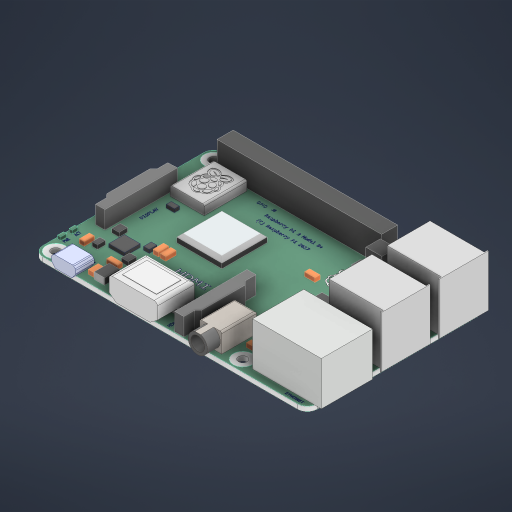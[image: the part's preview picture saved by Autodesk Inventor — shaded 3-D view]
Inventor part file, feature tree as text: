
AUTODESK INVENTOR PART (.ipt)
format: ipt  version: 2023 (Build 270158000, 158)  size: 3,770,368 bytes
history: native  units: mm
features: other x173, fillet x4, chamfer x1, extrude x1
ambient origin geometry x8: Origin, YZ Plane, XZ Plane, XY Plane, X Axis, Y Axis, Z Axis, Center Point
bodies: Solid1 (feature_tree), Solid2 (feature_tree), Solid3 (feature_tree), Solid4 (feature_tree), Solid5 (feature_tree), Solid6 (feature_tree), Solid7 (feature_tree), Solid8 (feature_tree), Solid9 (feature_tree), Solid10 (feature_tree), Solid11 (feature_tree), Solid12 (feature_tree), Solid13 (feature_tree), Solid14 (feature_tree), Solid15 (feature_tree), Solid16 (feature_tree), Solid17 (feature_tree), Solid18 (feature_tree), Solid19 (feature_tree), Solid20 (feature_tree), Solid21 (feature_tree), Solid22 (feature_tree), Solid23 (feature_tree), Solid24 (feature_tree), Solid25 (feature_tree), Solid26 (feature_tree), Solid27 (feature_tree), Solid28 (feature_tree), Solid29 (feature_tree), Solid30 (feature_tree), Solid31 (feature_tree), Solid32 (feature_tree), Solid33 (feature_tree), Solid34 (feature_tree), Solid35 (feature_tree), Solid36 (feature_tree), Solid37 (feature_tree), Solid38 (feature_tree), Solid39 (feature_tree), Solid40 (feature_tree), Solid41 (feature_tree), Solid42 (feature_tree), Solid43 (feature_tree), Solid44 (feature_tree), Solid45 (feature_tree), Solid46 (feature_tree), Solid47 (feature_tree), Solid48 (feature_tree), Solid49 (feature_tree), Solid50 (feature_tree), Solid51 (feature_tree), Solid52 (feature_tree), Solid53 (feature_tree), Solid54 (feature_tree), Solid55 (feature_tree), Solid56 (feature_tree), Solid57 (feature_tree), Solid58 (feature_tree), Solid59 (feature_tree), Solid60 (feature_tree), Solid61 (feature_tree), Solid62 (feature_tree), Solid63 (feature_tree), Solid64 (feature_tree), Solid65 (feature_tree), Solid66 (feature_tree), Solid67 (feature_tree), Solid68 (feature_tree), Solid69 (feature_tree), Solid70 (feature_tree), Solid71 (feature_tree), Solid72 (feature_tree), Solid73 (feature_tree), Solid74 (feature_tree), Solid75 (feature_tree), Solid76 (feature_tree), Solid77 (feature_tree), Solid78 (feature_tree), Solid79 (feature_tree), Solid80 (feature_tree), Solid81 (feature_tree), Solid82 (feature_tree), Solid83 (feature_tree), Solid84 (feature_tree), Solid85 (feature_tree), Solid86 (feature_tree), Solid87 (feature_tree), Solid88 (feature_tree), Solid89 (feature_tree), Solid90 (feature_tree), Solid91 (feature_tree), Solid92 (feature_tree), Solid93 (feature_tree), Solid94 (feature_tree), Solid95 (feature_tree), Solid96 (feature_tree), Solid97 (feature_tree), Solid98 (feature_tree), Solid99 (feature_tree), Solid100 (feature_tree), Solid101 (feature_tree), Solid102 (feature_tree), Solid103 (feature_tree), Solid104 (feature_tree), Solid105 (feature_tree), Solid106 (feature_tree), Solid107 (feature_tree), Solid108 (feature_tree), Solid109 (feature_tree), Solid110 (feature_tree), Solid111 (feature_tree), Solid112 (feature_tree), Solid113 (feature_tree), Solid114 (feature_tree), Solid115 (feature_tree), Solid116 (feature_tree), Solid117 (feature_tree), Solid118 (feature_tree), Solid119 (feature_tree), Solid120 (feature_tree), Solid121 (feature_tree), Solid122 (feature_tree), Solid123 (feature_tree), Solid124 (feature_tree), Solid125 (feature_tree), Solid126 (feature_tree), Solid127 (feature_tree), Solid128 (feature_tree), Solid129 (feature_tree), Solid130 (feature_tree), Solid131 (feature_tree), Solid132 (feature_tree), Solid133 (feature_tree), Solid134 (feature_tree), Solid135 (feature_tree), Solid136 (feature_tree), Solid137 (feature_tree), Solid138 (feature_tree), Solid139 (feature_tree), Solid140 (feature_tree), Solid141 (feature_tree), Solid142 (feature_tree), Solid143 (feature_tree), Solid144 (feature_tree), Solid145 (feature_tree), Solid146 (feature_tree), Solid147 (feature_tree), Solid148 (feature_tree), Solid149 (feature_tree), Solid150 (feature_tree), Solid151 (feature_tree), Solid152 (feature_tree), Solid153 (feature_tree), Solid154 (feature_tree), Solid155 (feature_tree), Solid156 (feature_tree), Solid157 (feature_tree), Solid158 (feature_tree), Solid159 (feature_tree), Solid160 (feature_tree), Solid161 (feature_tree), Solid162 (feature_tree), Solid163 (feature_tree), Solid164 (feature_tree), Solid165 (feature_tree), Solid166 (feature_tree), Solid167 (feature_tree), Solid168 (feature_tree), Solid169 (feature_tree), Solid170 (feature_tree), Solid171 (feature_tree), Solid172 (feature_tree), Solid173 (feature_tree), Solid174 (feature_tree), Solid175 (feature_tree), Solid176 (feature_tree), Solid177 (feature_tree), Solid178 (feature_tree), Solid179 (feature_tree)
feature tree (179):
  other  "Boss-Extrude4[1]"
  other  "Boss-Extrude5[1]"
  other  "Boss-Extrude5[2]"
  other  "Boss-Extrude6"
  other  "Boss-Extrude8[1]"
  other  "Boss-Extrude8[2]"
  fillet  "Fillet2"  [1 undecoded]
  fillet  "Fillet1"  [1 undecoded]
  other  "Boss-Extrude10"
  other  "Wrap1"
  chamfer  "Chamfer1"  [1 undecoded]
  fillet  "Fillet4"  [1 undecoded]
  other  "Boss-Extrude4[2]"
  extrude  "Extrude-Thin1"  [1 undecoded]
  other  "Cut-Extrude5[1]"
  other  "Boss-Extrude14[1]"
  other  "Boss-Extrude14[2]"
  other  "Boss-Extrude15[1]"
  other  "Boss-Extrude16[1]"
  other  "Boss-Extrude16[2]"
  other  "Boss-Extrude16[3]"
  other  "Boss-Extrude16[4]"
  other  "Boss-Extrude16[5]"
  other  "Boss-Extrude16[6]"
  other  "Boss-Extrude16[7]"
  other  "Boss-Extrude16[8]"
  other  "Boss-Extrude16[9]"
  other  "Boss-Extrude16[10]"
  other  "Boss-Extrude16[11]"
  other  "Boss-Extrude16[12]"
  other  "Boss-Extrude15[2]"
  other  "Boss-Extrude15[3]"
  other  "Boss-Extrude15[4]"
  other  "Boss-Extrude15[5]"
  other  "Boss-Extrude15[6]"
  other  "Boss-Extrude16[13]"
  other  "Boss-Extrude16[14]"
  other  "Boss-Extrude16[15]"
  other  "Boss-Extrude17"
  other  "Boss-Extrude15[7]"
  other  "Boss-Extrude18[1]"
  other  "Boss-Extrude18[2]"
  other  "Boss-Extrude18[3]"
  other  "Boss-Extrude18[4]"
  other  "Boss-Extrude18[5]"
  other  "Boss-Extrude18[6]"
  other  "Boss-Extrude18[7]"
  other  "Boss-Extrude18[8]"
  other  "Boss-Extrude18[9]"
  other  "Boss-Extrude18[10]"
  other  "Boss-Extrude18[11]"
  other  "Boss-Extrude18[12]"
  other  "Boss-Extrude18[13]"
  other  "Boss-Extrude18[14]"
  other  "Boss-Extrude18[15]"
  other  "Boss-Extrude18[16]"
  other  "Boss-Extrude18[17]"
  other  "Boss-Extrude18[18]"
  other  "Boss-Extrude18[19]"
  other  "Boss-Extrude18[20]"
  other  "Boss-Extrude18[21]"
  other  "Boss-Extrude18[22]"
  other  "Boss-Extrude18[23]"
  other  "Boss-Extrude18[24]"
  other  "Boss-Extrude18[25]"
  other  "Boss-Extrude18[26]"
  other  "Boss-Extrude18[27]"
  other  "Boss-Extrude18[28]"
  other  "Boss-Extrude18[29]"
  other  "Boss-Extrude18[30]"
  other  "Boss-Extrude18[31]"
  other  "Boss-Extrude18[32]"
  other  "Boss-Extrude18[33]"
  other  "Boss-Extrude18[34]"
  other  "Boss-Extrude18[35]"
  other  "Boss-Extrude18[36]"
  other  "Boss-Extrude18[37]"
  other  "Boss-Extrude18[38]"
  other  "Boss-Extrude18[39]"
  other  "Boss-Extrude18[40]"
  other  "Boss-Extrude18[41]"
  other  "Boss-Extrude18[42]"
  other  "Boss-Extrude18[43]"
  other  "Boss-Extrude18[44]"
  other  "Boss-Extrude18[45]"
  other  "Boss-Extrude18[46]"
  other  "Boss-Extrude18[47]"
  other  "Boss-Extrude19"
  other  "Boss-Extrude21[1]"
  other  "Boss-Extrude21[2]"
  other  "Boss-Extrude21[3]"
  other  "Boss-Extrude21[4]"
  other  "Boss-Extrude21[5]"
  other  "Boss-Extrude21[6]"
  other  "Boss-Extrude21[7]"
  other  "Boss-Extrude21[8]"
  other  "Boss-Extrude21[9]"
  other  "Boss-Extrude21[10]"
  other  "Boss-Extrude21[11]"
  other  "Boss-Extrude21[12]"
  other  "Boss-Extrude21[13]"
  other  "Boss-Extrude21[14]"
  other  "Boss-Extrude21[15]"
  other  "Boss-Extrude21[16]"
  other  "Boss-Extrude21[17]"
  other  "Boss-Extrude21[18]"
  other  "Boss-Extrude21[19]"
  other  "Boss-Extrude21[20]"
  other  "Boss-Extrude21[21]"
  other  "Boss-Extrude21[22]"
  other  "Boss-Extrude21[23]"
  other  "Boss-Extrude21[24]"
  other  "Boss-Extrude21[25]"
  other  "Boss-Extrude21[26]"
  other  "Boss-Extrude21[27]"
  other  "Boss-Extrude21[28]"
  other  "Boss-Extrude21[29]"
  other  "Boss-Extrude21[30]"
  other  "Boss-Extrude21[31]"
  other  "Boss-Extrude21[32]"
  other  "Boss-Extrude21[33]"
  other  "Boss-Extrude21[34]"
  other  "Boss-Extrude21[35]"
  other  "Boss-Extrude21[36]"
  other  "Boss-Extrude21[37]"
  other  "Boss-Extrude21[38]"
  other  "Boss-Extrude21[39]"
  other  "Boss-Extrude21[40]"
  other  "Boss-Extrude21[41]"
  other  "Boss-Extrude21[42]"
  other  "Boss-Extrude21[43]"
  other  "Boss-Extrude21[44]"
  other  "Boss-Extrude21[45]"
  other  "Boss-Extrude21[46]"
  other  "Boss-Extrude21[47]"
  other  "Boss-Extrude21[48]"
  other  "Boss-Extrude21[49]"
  other  "Boss-Extrude21[50]"
  other  "Boss-Extrude21[51]"
  other  "Boss-Extrude21[52]"
  other  "Boss-Extrude21[53]"
  other  "Boss-Extrude21[54]"
  other  "Boss-Extrude21[55]"
  other  "Boss-Extrude21[56]"
  other  "Boss-Extrude21[57]"
  other  "Boss-Extrude21[58]"
  other  "Boss-Extrude21[59]"
  other  "Boss-Extrude21[60]"
  other  "Boss-Extrude21[61]"
  other  "Boss-Extrude21[62]"
  other  "Boss-Extrude21[63]"
  other  "Boss-Extrude21[64]"
  other  "Boss-Extrude21[65]"
  other  "Boss-Extrude21[66]"
  other  "Boss-Extrude21[67]"
  other  "Boss-Extrude21[68]"
  other  "Boss-Extrude21[69]"
  other  "Boss-Extrude21[70]"
  other  "Boss-Extrude21[71]"
  other  "Boss-Extrude21[72]"
  other  "Boss-Extrude21[73]"
  other  "Boss-Extrude21[74]"
  other  "Boss-Extrude21[75]"
  other  "Boss-Extrude21[76]"
  other  "Boss-Extrude21[77]"
  other  "Boss-Extrude21[78]"
  other  "Boss-Extrude21[79]"
  other  "Boss-Extrude21[80]"
  other  "Boss-Extrude21[81]"
  other  "Boss-Extrude21[82]"
  other  "Boss-Extrude21[83]"
  other  "Boss-Extrude21[84]"
  other  "Boss-Extrude21[85]"
  other  "Boss-Extrude21[86]"
  other  "Boss-Extrude21[87]"
  other  "Boss-Extrude21[88]"
  other  "Boss-Extrude21[89]"
  other  "Boss-Extrude22"
  fillet  "Fillet7"  [1 undecoded]
note: 6 required parameter values undecoded (feature->parameter linkage not recoverable at this tier; creation-order binding heuristic only, values carry confidence <= 0.55)
